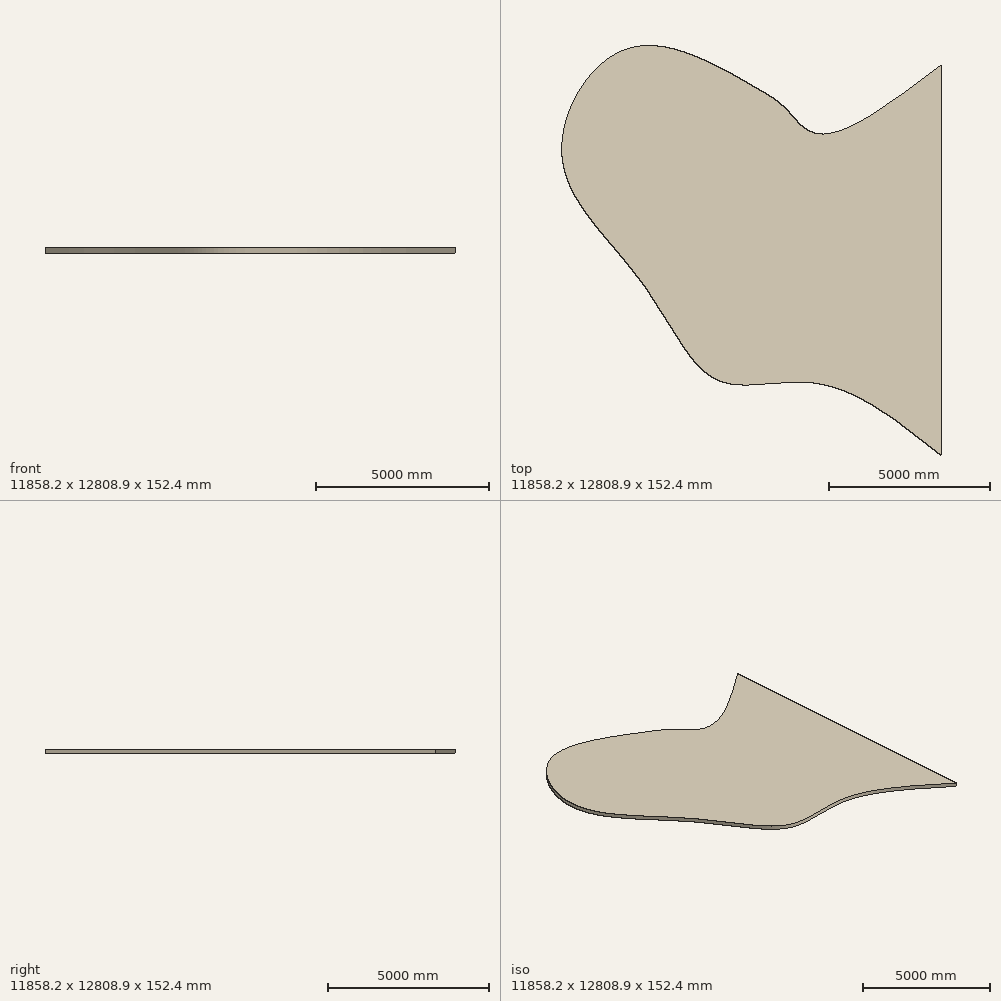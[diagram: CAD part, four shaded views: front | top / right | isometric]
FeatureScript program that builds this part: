
annotation { "Feature Type Name" : "Feature", "Feature Type Description" : "" }
export const myFeature = defineFeature(function(context is Context, id is Id, definition is map)
    precondition{}
    {
        {
            var Q0;
            Q0=qCreatedBy(makeId("Top.planeOp"),FACE);
            var sketch = newSketch(context, id + "F0", { "sketchPlane" : qUnion([Q0])});
            skLineSegment(sketch, "E0.right", {"start": v(3143.63, -6028.45) * mm, "end": v(3143.63, 6163.55) * mm});
            skPoint(sketch, "E1.5.internal.snap0", {"position": v(-1428.37, 6163.55) * mm});
            skLineSegment(sketch, "E2", {"start": v(2198.96, -6028.45) * mm, "end": v(3143.63, -6028.45) * mm});
            skFitSpline(sketch, "E3", {"points": [v(3143.63, -6028.45) * mm, v(-785.58, -3769.02) * mm, v(-3840.71, -3676.56) * mm, v(-6166.33, -674.62) * mm, v(-8701.93, 3272.5) * mm, v(-6788.58, 6628.48) * mm, v(-1768.38, 4945.28) * mm], "startDerivative": vector(-22783.55, 18256.82) * mm, "endDerivative": vector(33069.26, -19821.2) * mm});
            skFitSpline(sketch, "E4", {"points": [v(-1768.38, 4945.28) * mm, v(-639.94, 4016.92) * mm, v(3143.63, 6163.55) * mm], "startDerivative": vector(2543.23, -3616.4) * mm, "endDerivative": vector(6894.72, 5265) * mm});
            skSolve(sketch);
        }
        {
            var Q0;
            Q0 = qSketchRegion(id + "F0", true);
            extrude(context, id + "F1", {"entities" : qUnion([Q0]), "depth" : 152.4 * mm});
        }
        {
            var Q0;
            Q0=makeQuery(id+"F1.opExtrude","SWEPT_EDGE",EDGE,{"disambiguationData":[OSD([sQuery(id+"F0.wireOp",EDGE,"E3"),sQuery(id+"F0.wireOp",EDGE,"E4")])]});
            fillet(context, id + "F2", {"entities" : qUnion([Q0]), "radius" : 3048 * mm, "tangentPropagation" : true, "allowEdgeOverflow" : false});
        }
    });
